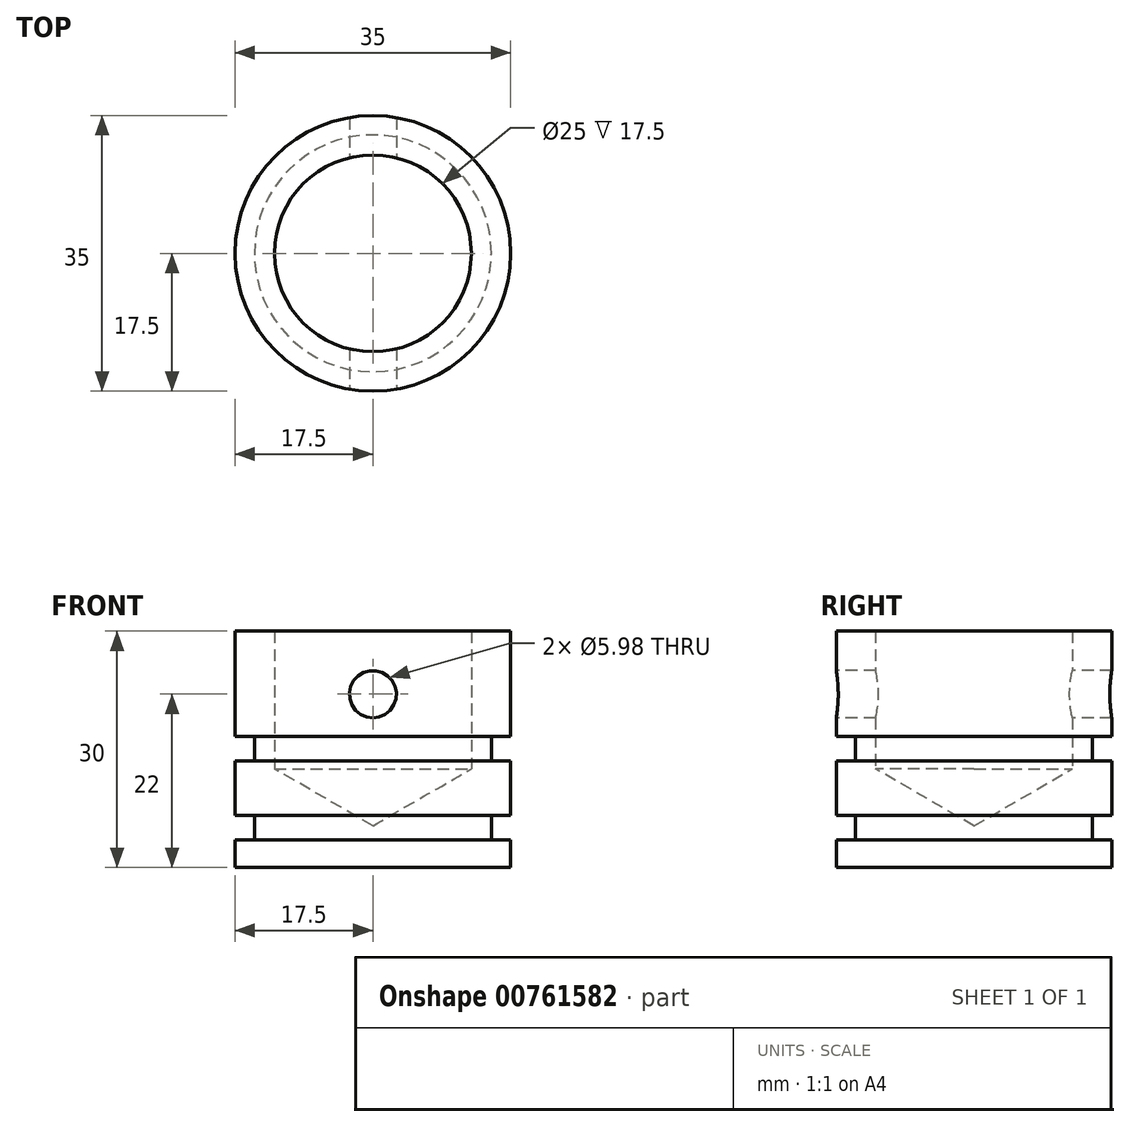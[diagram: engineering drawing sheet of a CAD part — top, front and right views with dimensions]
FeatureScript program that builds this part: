
annotation { "Feature Type Name" : "Feature", "Feature Type Description" : "" }
export const myFeature = defineFeature(function(context is Context, id is Id, definition is map)
    precondition{}
    {
        {
            var Q0;
            Q0=qCreatedBy(makeId("Front.planeOp"),FACE);
            var sketch = newSketch(context, id + "F0", { "sketchPlane" : qUnion([Q0])});
            skLineSegment(sketch, "E0", {"start": v(0, 0) * mm, "end": v(0, 5.28) * mm});
            skLineSegment(sketch, "E1", {"start": v(0, 5.28) * mm, "end": v(-12.5, 12.5) * mm});
            skLineSegment(sketch, "E2", {"start": v(-12.5, 12.5) * mm, "end": v(-12.5, 30) * mm});
            skLineSegment(sketch, "E3", {"start": v(-12.5, 30) * mm, "end": v(-17.5, 30) * mm});
            skLineSegment(sketch, "E4", {"start": v(-17.5, 30) * mm, "end": v(-17.5, 16.6) * mm});
            skLineSegment(sketch, "E5", {"start": v(-17.5, 16.6) * mm, "end": v(-15.05, 16.6) * mm});
            skLineSegment(sketch, "E6", {"start": v(-15.05, 16.6) * mm, "end": v(-15.05, 13.5) * mm});
            skLineSegment(sketch, "E7", {"start": v(-15.05, 13.5) * mm, "end": v(-17.5, 13.5) * mm});
            skLineSegment(sketch, "E8", {"start": v(-17.5, 13.5) * mm, "end": v(-17.5, 6.6) * mm});
            skLineSegment(sketch, "E9", {"start": v(-17.5, 6.6) * mm, "end": v(-15.05, 6.6) * mm});
            skLineSegment(sketch, "E10", {"start": v(-15.05, 6.6) * mm, "end": v(-15.05, 3.5) * mm});
            skLineSegment(sketch, "E11", {"start": v(-15.05, 3.5) * mm, "end": v(-17.5, 3.5) * mm});
            skLineSegment(sketch, "E12", {"start": v(-17.5, 3.5) * mm, "end": v(-17.5, 0) * mm});
            skLineSegment(sketch, "E13", {"start": v(-17.5, 0) * mm, "end": v(0, 0) * mm});
            skSolve(sketch);
        }
        {
            var Q0;
            Q0 = qSketchRegion(id + "F0", true);
            var Q1;
            Q1=sQuery(id+"F0.wireOp",EDGE,"E0");
            revolve(context, id + "F1", {"surfaceOperationType" : NewSurfaceOperationType.NEW, "entities" : qUnion([Q0]), "axis" : qUnion([Q1]), "revolveType" : RevolveType.FULL});
        }
        {
            var Q0;
            Q0=qCreatedBy(makeId("Front.planeOp"),FACE);
            var sketch = newSketch(context, id + "F2", { "sketchPlane" : qUnion([Q0])});
            skCircle(sketch, "E14", {"center": v(0, 22) * mm, "radius": 3 * mm});
            skSolve(sketch);
        }
        {
            var Q0;
            Q0 = qSketchRegion(id + "F2", true);
            extrude(context, id + "F3", {"entities" : qUnion([Q0]), "operationType" : NewBodyOperationType.REMOVE, "endBound" : BoundingType.SYMMETRIC, "oppositeDirection" : true, "depth" : 40 * mm, "offsetDistance" : 25 * mm});
        }
    });
